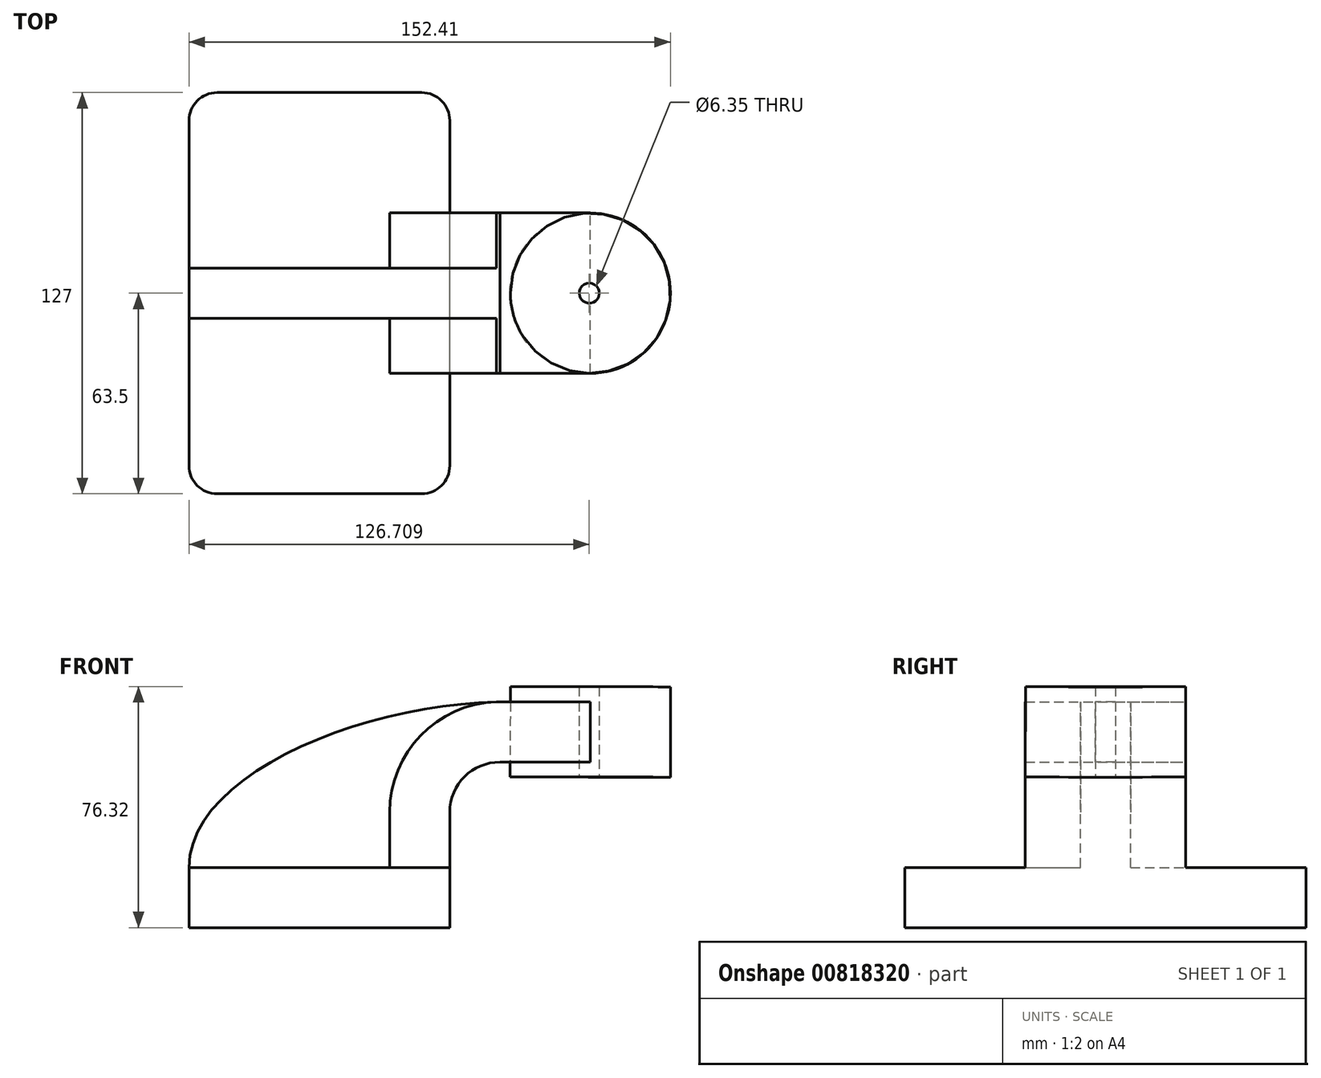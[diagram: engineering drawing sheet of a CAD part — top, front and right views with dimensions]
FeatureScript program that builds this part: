
annotation { "Feature Type Name" : "Feature", "Feature Type Description" : "" }
export const myFeature = defineFeature(function(context is Context, id is Id, definition is map)
    precondition{}
    {
        {
            var Q0;
            Q0=qCreatedBy(makeId("Front.planeOp"),FACE);
            var sketch = newSketch(context, id + "F0", { "sketchPlane" : qUnion([Q0])});
            skLineSegment(sketch, "E0.bottom", {"start": v(-41.28, 9.52) * mm, "end": v(41.28, 9.53) * mm});
            skLineSegment(sketch, "E0.top", {"start": v(-41.28, -9.53) * mm, "end": v(41.28, -9.53) * mm});
            skLineSegment(sketch, "E0.left", {"start": v(-41.28, 9.52) * mm, "end": v(-41.27, -9.53) * mm});
            skLineSegment(sketch, "E0.right", {"start": v(41.28, 9.53) * mm, "end": v(41.28, -9.52) * mm});
            skPoint(sketch, "E0.middle", {"position": v(0, 0) * mm});
            skLineSegment(sketch, "E1.bottom", {"start": v(60.32, 66.68) * mm, "end": v(111.12, 66.68) * mm});
            skLineSegment(sketch, "E1.top", {"start": v(60.32, 38.1) * mm, "end": v(111.12, 38.1) * mm});
            skLineSegment(sketch, "E1.left", {"start": v(60.32, 66.68) * mm, "end": v(60.32, 38.1) * mm});
            skLineSegment(sketch, "E1.right", {"start": v(111.12, 66.68) * mm, "end": v(111.12, 38.1) * mm});
            skPoint(sketch, "E1.middle", {"position": v(85.72, 52.39) * mm});
            skLineSegment(sketch, "E2", {"start": v(41.27, 9.53) * mm, "end": v(41.27, 27) * mm});
            skArc(sketch, "E3", {"start": v(57.15, 42.88) * mm, "mid": v(45.92, 38.23) * mm, "end": v(41.27, 27) * mm});
            skLineSegment(sketch, "E4", {"start": v(57.15, 42.88) * mm, "end": v(85.8, 42.88) * mm});
            skLineSegment(sketch, "E5.0", {"start": v(57.15, 61.93) * mm, "end": v(85.8, 61.93) * mm});
            skArc(sketch, "E5.1", {"start": v(57.15, 61.93) * mm, "mid": v(32.45, 51.7) * mm, "end": v(22.22, 27) * mm});
            skLineSegment(sketch, "E5.2", {"start": v(22.22, 9.53) * mm, "end": v(22.22, 27) * mm});
            skFitSpline(sketch, "E6", {"points": [v(-41.28, 9.52) * mm, v(57.15, 61.93) * mm], "startDerivative": vector(0.44, 90.28) * mm, "endDerivative": vector(126.5, 1.45) * mm});
            skLineSegment(sketch, "E7", {"start": v(85.72, 38.1) * mm, "end": v(85.8, 66.68) * mm});
            skSolve(sketch);
        }
        {
            var Q0;
            Q0=makeQuery(id+"F0.imprint","IMPRINT",FACE,{"disambiguationData":[TD([[makeQuery(id+"F0.imprint","IMPRINT",EDGE,{"derivedFrom":sQuery(id+"F0.wireOp",EDGE,"E0.top")}),1.0]])]});
            extrude(context, id + "F1", {"entities" : qUnion([Q0]), "endBound" : BoundingType.SYMMETRIC, "depth" : 127 * mm, "offsetDistance" : 25.4 * mm});
        }
        {
            var Q0;
            {var subQ0=sQuery(id+"F0.wireOp",EDGE,"E5.0");var subQ1=sQuery(id+"F0.wireOp",EDGE,"E1.left");var subQ2=makeQuery(id+"F0.imprint","INTERSECT",VERTEX,{"derivedFrom":[subQ1,subQ0]});Q0=makeQuery(id+"F0.imprint","IMPRINT",FACE,{"disambiguationData":[TD([[makeQuery(id+"F0.imprint","IMPRINT",EDGE,{"disambiguationData":[TD([[subQ2,-1.0]])],"derivedFrom":subQ1}),1.0]])]});}
            var Q1;
            {var subQ1=sQuery(id+"F0.wireOp",EDGE,"E2");Q1=makeQuery(id+"F0.imprint","IMPRINT",FACE,{"disambiguationData":[TD([[makeQuery(id+"F0.imprint","IMPRINT",EDGE,{"derivedFrom":subQ1}),1.0]])]});}
            extrude(context, id + "F2", {"entities" : qUnion([Q0, Q1]), "operationType" : NewBodyOperationType.ADD, "endBound" : BoundingType.SYMMETRIC, "depth" : 50.8 * mm, "offsetDistance" : 25.4 * mm});
        }
        {
            var Q0;
            {var subQ3=sQuery(id+"F0.wireOp",EDGE,"E5.2");Q0=makeQuery(id+"F0.imprint","IMPRINT",FACE,{"disambiguationData":[TD([[makeQuery(id+"F0.imprint","IMPRINT",EDGE,{"derivedFrom":subQ3}),1.0]])]});}
            extrude(context, id + "F3", {"entities" : qUnion([Q0]), "operationType" : NewBodyOperationType.ADD, "endBound" : BoundingType.SYMMETRIC, "depth" : 15.88 * mm, "offsetDistance" : 25.4 * mm});
        }
        {
            var Q0;
            {var subQ4=sQuery(id+"F0.wireOp",EDGE,"E1.right");Q0=makeQuery(id+"F0.imprint","IMPRINT",FACE,{"disambiguationData":[TD([[makeQuery(id+"F0.imprint","IMPRINT",EDGE,{"derivedFrom":subQ4}),-1.0]])]});}
            var Q1;
            Q1=sQuery(id+"F0.wireOp",EDGE,"E7");
            revolve(context, id + "F4", {"surfaceOperationType" : NewSurfaceOperationType.NEW, "entities" : qUnion([Q0]), "axis" : qUnion([Q1]), "revolveType" : RevolveType.FULL});
        }
        {
            var Q0;
            Q0=makeQuery(id+"F1.opExtrude","CAP_EDGE",EDGE,{"disambiguationData":[OSD([sQuery(id+"F0.wireOp",EDGE,"E0.left")])],"isStart":false});
            var Q1;
            Q1=makeQuery(id+"F1.opExtrude","CAP_EDGE",EDGE,{"disambiguationData":[OSD([sQuery(id+"F0.wireOp",EDGE,"E0.right")])],"isStart":false});
            var Q2;
            Q2=makeQuery(id+"F1.opExtrude","CAP_EDGE",EDGE,{"disambiguationData":[OSD([sQuery(id+"F0.wireOp",EDGE,"E0.right")])],"isStart":true});
            var Q3;
            Q3=makeQuery(id+"F1.opExtrude","CAP_EDGE",EDGE,{"disambiguationData":[OSD([sQuery(id+"F0.wireOp",EDGE,"E0.left")])],"isStart":true});
            fillet(context, id + "F5", {"entities" : qUnion([Q0, Q1, Q2, Q3]), "radius" : 8.9 * mm, "tangentPropagation" : true, "allowEdgeOverflow" : false});
        }
        {
            var Q0;
            Q0=qCreatedBy(makeId("Top.planeOp"),FACE);
            var sketch = newSketch(context, id + "F6", { "sketchPlane" : qUnion([Q0])});
            skPoint(sketch, "E8", {"position": v(85.43, 0) * mm});
            skSolve(sketch);
        }
        {
            var Q0;
            Q0=sQuery(id+"F6.wireOp",VERTEX,"E8");
            var Q1;
            Q1=makeQuery(id+"F4.opRevolve","SWEPT_BODY",BODY,{"disambiguationData":[OSD([sQuery(id+"F0.wireOp",EDGE,"E1.bottom"),sQuery(id+"F0.wireOp",EDGE,"E1.top"),sQuery(id+"F0.wireOp",EDGE,"E1.right"),sQuery(id+"F0.wireOp",EDGE,"E7")])]});
            var Q2;
            Q2=makeQuery(id+"F1.opExtrude","SWEPT_BODY",BODY,{"disambiguationData":[OSD([sQuery(id+"F0.wireOp",EDGE,"E0.bottom"),sQuery(id+"F0.wireOp",EDGE,"E0.top"),sQuery(id+"F0.wireOp",EDGE,"E0.left"),sQuery(id+"F0.wireOp",EDGE,"E0.right")])]});
            hole(context, id + "F7", {"style" : HoleStyle.SIMPLE, "endStyle" : HoleEndStyle.THROUGH, "oppositeDirection" : true, "holeDiameter" : 6.35 * mm, "majorDiameter" : 6.35 * mm, "isTappedThrough" : true, "tappedDepth" : 12.7 * mm, "tapClearance" : 3, "locations" : qUnion([Q0]), "scope" : qUnion([Q1, Q2])});
        }
    });
